# Revit family: FU_Stool_Sandler_Varya 0067
name_source: partatom
category: Furniture
units: mm (PartAtom-declared; Revit-internal decimal feet)

## family parameters
Always vertical = Yes
Cut with Voids When Loaded = No
OmniClass Number = 23.40.20.00
OmniClass Title = General Furniture and Specialties
Room Calculation Point = No
Shared = No
Work Plane-Based = No

## types (1)
- Varya 0067
    Default Elevation = 0 mm  [stored 0 ft]
    Depth = 490 mm  [stored 1.60761 ft]
    Description = High back counterstool with polypropylene shell, round steel tube sled base and upholstered seat. Greenguard Certified.
    Height = 1020 mm  [stored 3.34646 ft]
    Manufacturer = Sandler
    Model = Varya 0067
    URL = https://www.sandlerseating.com
    Width = 465 mm  [stored 1.52559 ft]

note: [stored X ft] marks values corroborated as IEEE doubles in the binary element streams (Revit-internal decimal feet)

## geometry (parser evidence)
native form markers: Sweep x7
no freeform markers — native parametric forms only
